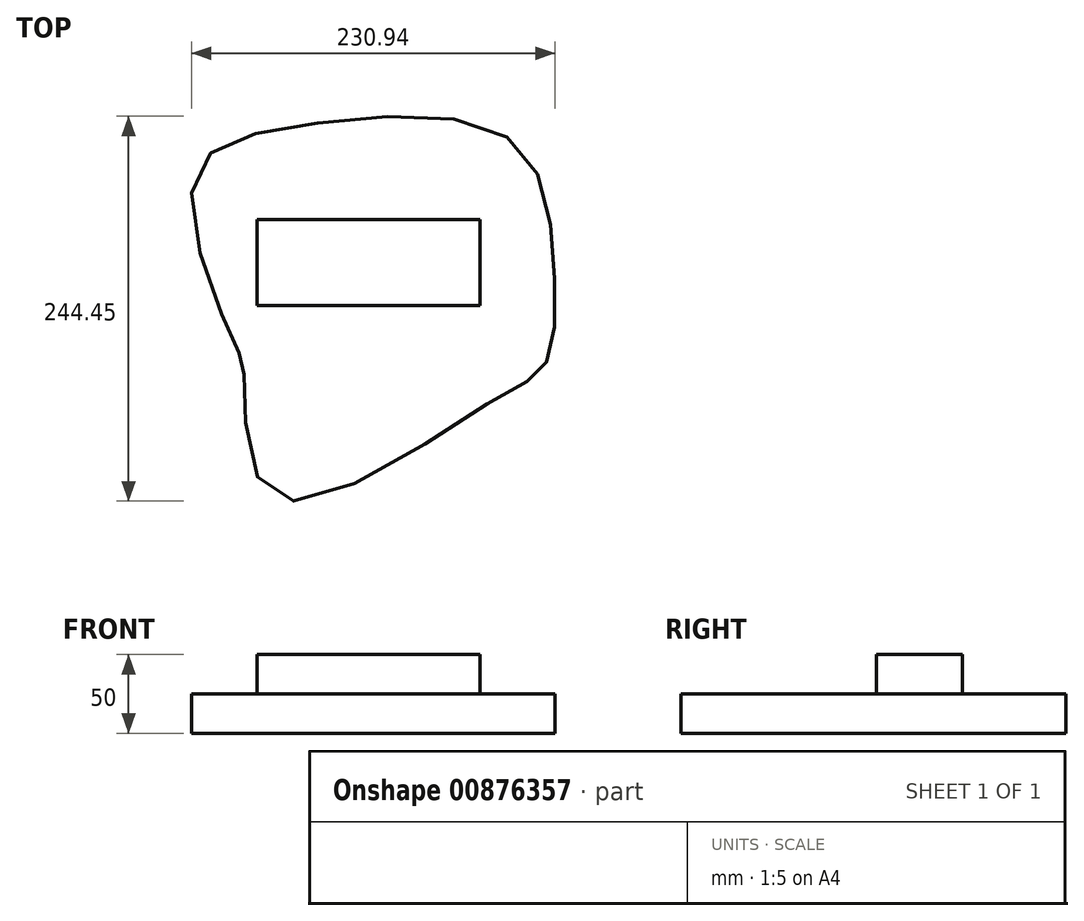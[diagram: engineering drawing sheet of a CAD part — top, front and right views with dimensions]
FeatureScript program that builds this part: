
annotation { "Feature Type Name" : "Feature", "Feature Type Description" : "" }
export const myFeature = defineFeature(function(context is Context, id is Id, definition is map)
    precondition{}
    {
        {
            var Q0;
            Q0=qCreatedBy(makeId("Top.planeOp"),FACE);
            var sketch = newSketch(context, id + "F0", { "sketchPlane" : qUnion([Q0])});
            skFitSpline(sketch, "E0", {"points": [v(-89, -43.6) * mm, v(-93.92, -26.44) * mm, v(-121.37, 78.84) * mm, v(-51.51, 114.73) * mm, v(80.56, 105.4) * mm, v(107.77, 25.55) * mm, v(102.85, -36.2) * mm, v(69.77, -59.73) * mm, v(-69.68, -121.36) * mm, v(-89, -43.6) * mm]});
            skSolve(sketch);
        }
        {
            var Q0;
            Q0=makeQuery(id+"F0.imprint","IMPRINT",FACE,{"disambiguationData":[TD([[makeQuery(id+"F0.imprint","IMPRINT",EDGE,{"derivedFrom":sQuery(id+"F0.wireOp",EDGE,"E0")}),-1.0]])]});
            extrude(context, id + "F1", {"entities" : qUnion([Q0]), "depth" : 25 * mm, "offsetDistance" : 25 * mm});
        }
        {
            var Q0;
            Q0=makeQuery(id+"F1.opExtrude","CAP_FACE",FACE,{"disambiguationData":[OSD([sQuery(id+"F0.wireOp",EDGE,"E0")])],"isStart":false});
            var sketch = newSketch(context, id + "F2", { "sketchPlane" : qUnion([Q0])});
            skLineSegment(sketch, "E1.bottom", {"start": v(-80.68, 54.56) * mm, "end": v(60.68, 54.56) * mm});
            skLineSegment(sketch, "E1.top", {"start": v(-80.68, 0) * mm, "end": v(60.68, 0) * mm});
            skLineSegment(sketch, "E1.left", {"start": v(-80.68, 54.56) * mm, "end": v(-80.68, 0) * mm});
            skLineSegment(sketch, "E1.right", {"start": v(60.68, 54.56) * mm, "end": v(60.68, 0) * mm});
            skSolve(sketch);
        }
        {
            var Q0;
            Q0=makeQuery(id+"F2.imprint","IMPRINT",FACE,{"disambiguationData":[TD([[makeQuery(id+"F2.imprint","IMPRINT",EDGE,{"derivedFrom":sQuery(id+"F2.wireOp",EDGE,"E1.bottom")}),-1.0]])]});
            extrude(context, id + "F3", {"entities" : qUnion([Q0]), "operationType" : NewBodyOperationType.ADD, "depth" : 25 * mm, "offsetDistance" : 25 * mm});
        }
    });
